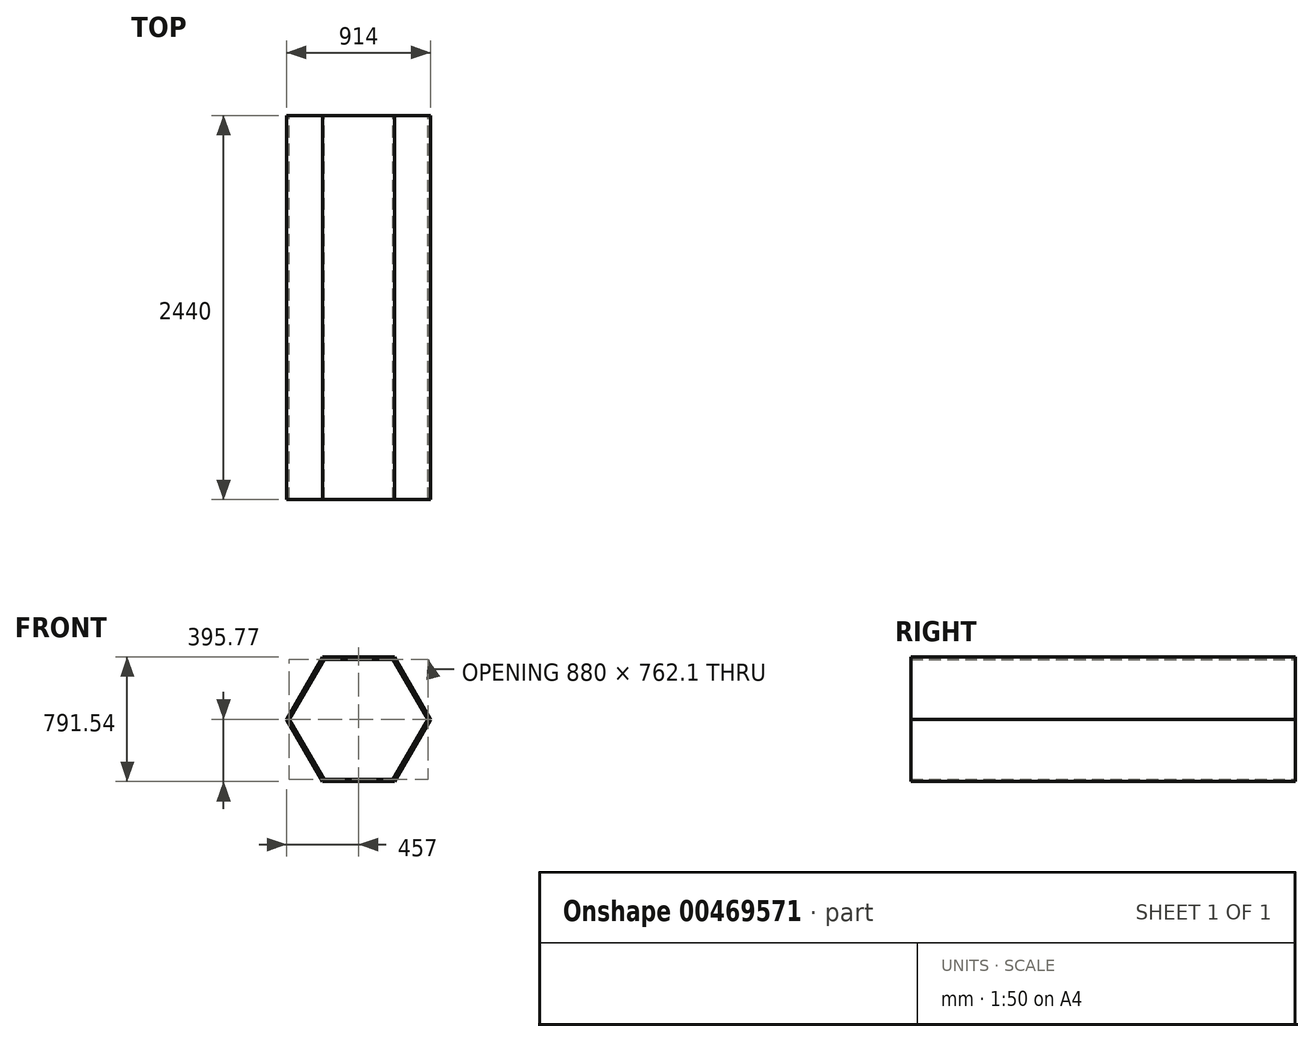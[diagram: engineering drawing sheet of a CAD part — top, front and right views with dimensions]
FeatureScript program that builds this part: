
annotation { "Feature Type Name" : "Feature", "Feature Type Description" : "" }
export const myFeature = defineFeature(function(context is Context, id is Id, definition is map)
    precondition{}
    {
        {
            var Q0;
            Q0=qCreatedBy(makeId("Front.planeOp"),FACE);
            var sketch = newSketch(context, id + "F0", { "sketchPlane" : qUnion([Q0]), "disableImprinting" : false});
            skCircle(sketch, "E0.cCircle", {"center": v(0, 0) * mm, "radius": 395.77 * mm, "construction": true});
            skLineSegment(sketch, "E0.0", {"start": v(228.5, -395.77) * mm, "end": v(-228.5, -395.77) * mm});
            skLineSegment(sketch, "E0.1", {"start": v(-228.5, -395.77) * mm, "end": v(-457, 0) * mm});
            skLineSegment(sketch, "E0.2", {"start": v(-457, 0) * mm, "end": v(-228.5, 395.77) * mm});
            skLineSegment(sketch, "E0.3", {"start": v(-228.5, 395.77) * mm, "end": v(228.5, 395.77) * mm});
            skLineSegment(sketch, "E0.4", {"start": v(228.5, 395.77) * mm, "end": v(457, 0) * mm});
            skLineSegment(sketch, "E0.5", {"start": v(457, 0) * mm, "end": v(228.5, -395.77) * mm});
            skPoint(sketch, "E0.0.midPoint", {"position": v(0, -395.77) * mm});
            skCircle(sketch, "E1.cCircle", {"center": v(0, 0) * mm, "radius": 381.05 * mm, "construction": true});
            skLineSegment(sketch, "E1.0", {"start": v(220, -381.05) * mm, "end": v(-220, -381.05) * mm});
            skLineSegment(sketch, "E1.1", {"start": v(-220, -381.05) * mm, "end": v(-440, 0) * mm});
            skLineSegment(sketch, "E1.2", {"start": v(-440, 0) * mm, "end": v(-220, 381.05) * mm});
            skLineSegment(sketch, "E1.3", {"start": v(-220, 381.05) * mm, "end": v(220, 381.05) * mm});
            skLineSegment(sketch, "E1.4", {"start": v(220, 381.05) * mm, "end": v(440, 0) * mm});
            skLineSegment(sketch, "E1.5", {"start": v(440, 0) * mm, "end": v(220, -381.05) * mm});
            skPoint(sketch, "E1.0.midPoint", {"position": v(0, -381.05) * mm});
            skSolve(sketch);
        }
        {
            var Q0;
            Q0=makeQuery(id+"F0.imprint","IMPRINT",FACE,{"disambiguationData":[TD([[makeQuery(id+"F0.imprint","IMPRINT",EDGE,{"derivedFrom":sQuery(id+"F0.wireOp",EDGE,"E0.0")}),-1.0]])]});
            extrude(context, id + "F1", {"entities" : qUnion([Q0]), "depth" : 2440 * mm, "offsetDistance" : 25 * mm});
        }
    });
